# Revit family: Interceptor_Solids_Sediment-Zurn-Z1187
name_source: partatom
category: Plumbing Fixtures
units: mm (PartAtom-declared; Revit-internal decimal feet)

## family parameters
Always vertical = Yes
Cut with Voids When Loaded = No
Maintain Annotation Orientation = No
OmniClass Number = 23.45.30.00
OmniClass Title = Washing and Waste Disposal Equipment
Part Type = Normal
Room Calculation Point = No
Round Connector Dimension = Use Radius
Shared = No
Work Plane-Based = No

## types (7) — shared parameters
A1_Vent Size (Inner Diameter) = 2.067 "
A1_Vent Size (Nominal Diameter) = 2 "
A1_Vent Size (Nominal Radius) = 1 "
A1_Vent Size (Outer Diameter) = 2.375 "
A_Pipe Size (Inner Diameter) = 4.026 "
A_Pipe Size (Nominal Diameter) = 4 "
A_Pipe Size (Nominal Radius) = 2 "
A_Pipe Size (Outer Diameter) = 4.5 "
Assembly Code = D2090300
CW Connection = No
Default Elevation = 20 "
Description = SAND AND SEDIMENT INTERCEPTOR
HW Connection = No
Height (From Base to Inlet/Outlet) = 38 "
Height (From Base to Vents) = 48 "
Main Material = Fabricated Steel - Zurn- Acid Resistant Coated
Manufacturer = Zurn Water, LLC
Manufacurer Brand = Zurn
Model = Z1187
Modified Date = 01/13/2026
Product Documentation Link = https://files.zurn.com
Product Installation Sheet URL = https://files.zurn.com
Product Page URL = https://www.zurn.com
Product data url = https://www.bimobject.com
Total Height of Body = 60 "
URL = www.zurn.com
Vent Connection = No
WFU = 1
Waste Connection = Yes
Width of Body = 36 "
zero-valued in all types: CWFU, HWFU

## per-type parameters (varying)
| type | Approx Wt. (Lbs) | F_Length | F_Length/4 (For A1_Vents) | F_Length/4 (For A1_Vents)_1st & 4th Vents | Volume (Cubic Ft.) |
| Z1187-Size_300 | 1600 " | 60 " | 15 " | 7.5 " | 43 CF |
| Z1187-Size_400 | 1750 " | 72 " | 18 " | 9 " | 54 CF |
| Z1187-Size_500 | 2100 " | 96 " | 24 " | 12 " | 72 CF |
| Z1187-Size_600 | 2500 " | 108 " | 27 " | 13.5 " | 81 CF |
| Z1187-Size_700 | 2700 " | 120 " | 30 " | 15 " | 90 CF |
| Z1187-Size_800 | 3000 " | 144 " | 36 " | 18 " | 108 CF |
| Z1187-Size_1000 | 3640 " | 180 " | 45 " | 22.5 " | 135 CF |

note: column(s) folded — value = type name in every type: Type Comments

## geometry (parser evidence)
native form markers: Sweep x3
no freeform markers — native parametric forms only
